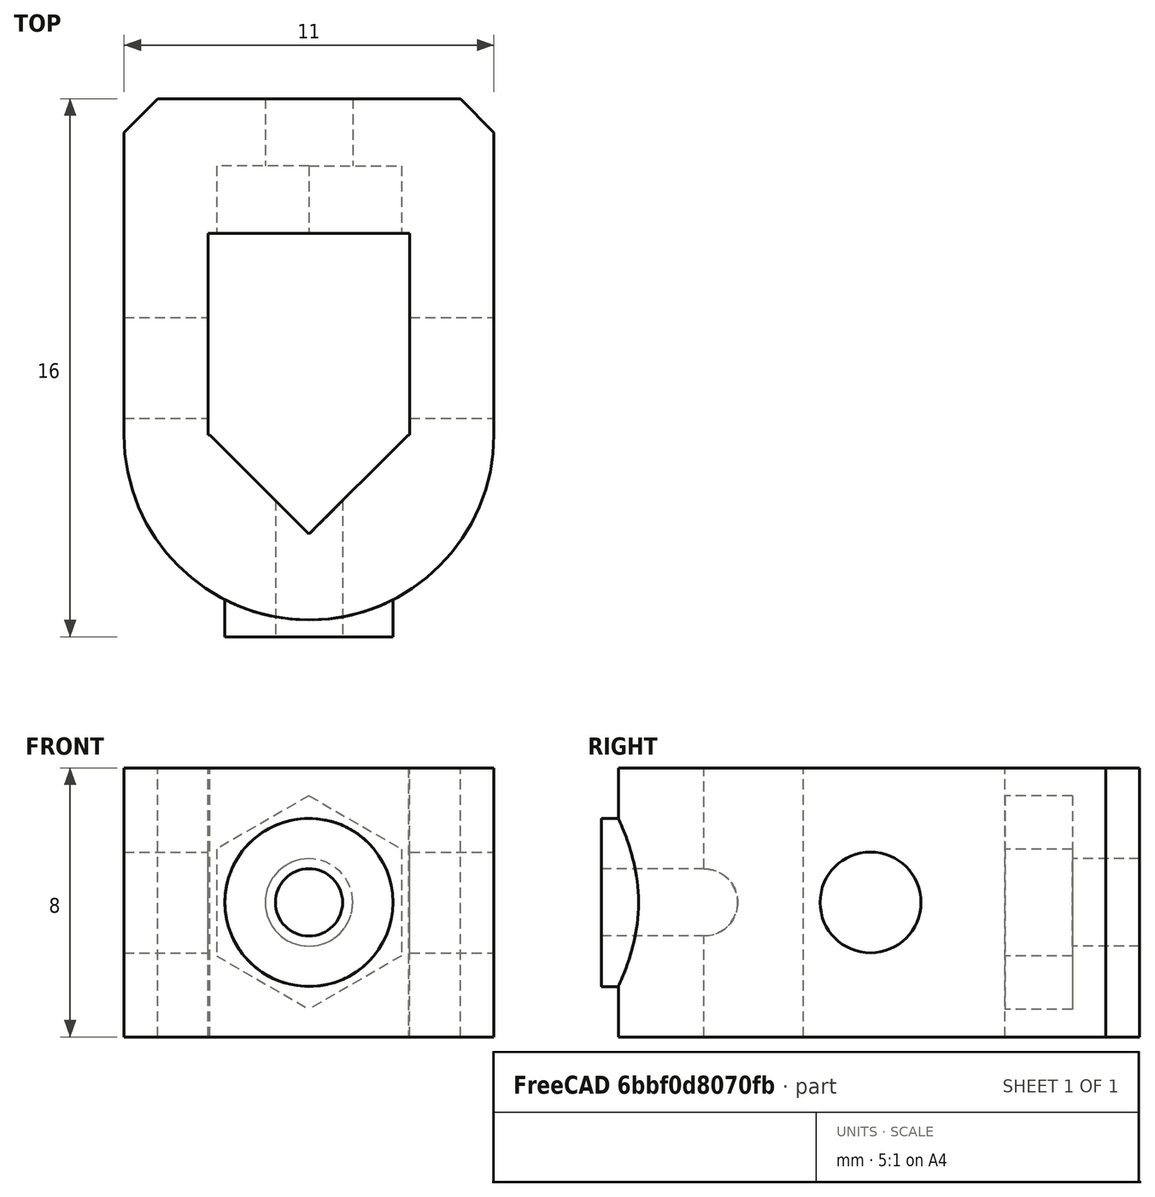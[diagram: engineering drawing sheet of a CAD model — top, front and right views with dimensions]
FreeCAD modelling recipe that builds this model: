
FCSTD DOCUMENT  (FreeCAD 0.15R4671 (Git))
Label: line_fastener_for_bolt
License: CC-BY 3.0
LicenseURL: http://creativecommons.org/licenses/by/3.0/
objects: Part::Cylinder×5, Part::Box×3, Part::MultiFuse×3, Part::Extrusion×1, Part::Mirroring×1, Part::Chamfer×1, Part::Cut×1
note: 15 computed .brp shape members not serialized (recipe doc carries the construction recipe); baked Part::Feature solids carry a one-line shape summary decoded from their .brp

FEATURE [Part::Cylinder] Cylinder
  Angle = 360
  Height = 8
  Placement = pos=(0,-2,0) rot=(0,0,1;0rad)
  Radius = 5.5
FEATURE [Part::Box] Box  label="Cube"
  Height = 14
  Length = 6
  Placement = pos=(-3,-2,-2) rot=(0,0,1;0rad)
  Width = 6
FEATURE [Part::Cylinder] Cylinder002
  Angle = 360
  Height = 10
  Placement = pos=(0,0,4) rot=(1,0,0;1.5708rad)
  Radius = 1
FEATURE [Part::Cylinder] Cylinder003
  Angle = 360
  Height = 8
  Placement = pos=(0,0,4) rot=(1,0,0;1.5708rad)
  Radius = 2.5
FEATURE [Part::Box] Box001  label="Cube001"
  Height = 8
  Length = 11
  Placement = pos=(-5.5,-2,0) rot=(0,0,1;0rad)
  Width = 10
FEATURE [Part::Cylinder] Cylinder005
  Angle = 360
  Height = 10
  Placement = pos=(0,10,4) rot=(1,0,0;1.5708rad)
  Radius = 1.3
FEATURE [Part::Extrusion] Extrude
  Dir = (0,0,2)
  Solid = true
FEATURE [Part::Mirroring] Part__Mirroring  label="Extrude (Mirror #1)"
  Base = (0,0,0)
  Normal = (1,0,0)
  Source = -> Extrude
FEATURE [Part::MultiFuse] Fusion002
  Placement = pos=(0,6,4) rot=(1,0,0;1.5708rad)
  Shapes = -> [Part__Mirroring,Extrude]
FEATURE [Part::Chamfer] Chamfer
  Base = -> Box001
  Edges = 2 edges r=1: [Edge3,Edge7]
FEATURE [Part::Cylinder] Cylinder006
  Angle = 360
  Height = 20
  Placement = pos=(-9,0,4) rot=(0,1,0;1.5708rad)
  Radius = 1.5
FEATURE [Part::MultiFuse] Fusion
  Shapes = -> [Cylinder,Cylinder003,Chamfer]
FEATURE [Part::Box] Box002  label="Cube002"
  Height = 14
  Length = 4.2
  Placement = pos=(0,-4.95,-2) rot=(0,0,1;0.785398rad)
  Width = 4.2
FEATURE [Part::MultiFuse] Fusion003
  Shapes = -> [Box002,Cylinder006,Cylinder002,Cylinder005,Box,Fusion002]
FEATURE [Part::Cut] Cut
  Base = -> Fusion
  Tool = -> Fusion003
